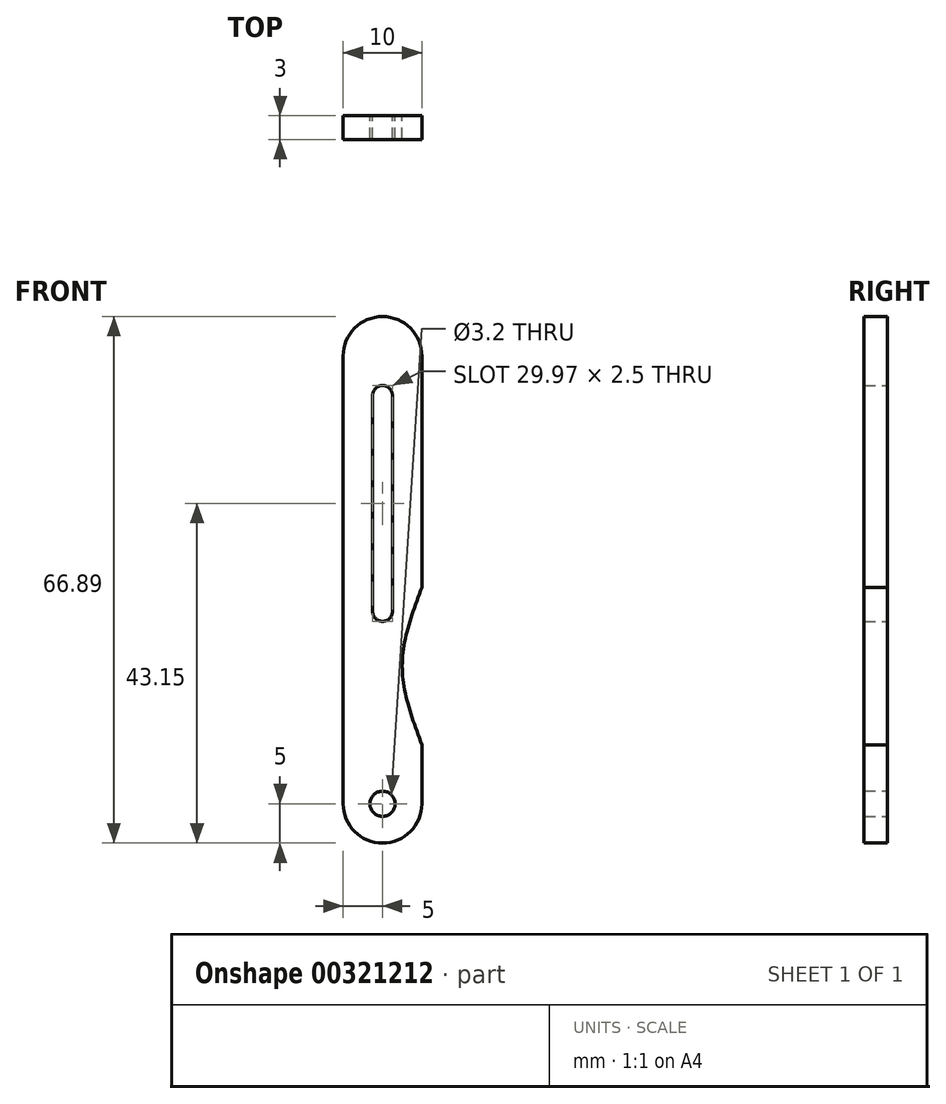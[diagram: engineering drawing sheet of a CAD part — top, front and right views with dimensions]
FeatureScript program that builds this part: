
annotation { "Feature Type Name" : "Feature", "Feature Type Description" : "" }
export const myFeature = defineFeature(function(context is Context, id is Id, definition is map)
    precondition{}
    {
        {
            var Q0;
            Q0=qCreatedBy(makeId("Front.planeOp"),FACE);
            var sketch = newSketch(context, id + "F0", { "sketchPlane" : qUnion([Q0])});
            skCircle(sketch, "E0", {"center": v(0, 17.5) * mm, "radius": 7 * mm, "construction": true});
            skLineSegment(sketch, "E1.bottom", {"start": v(2.5, 27.5) * mm, "end": v(-2.5, 27.5) * mm, "construction": true});
            skLineSegment(sketch, "E1.top", {"start": v(2.5, 7.5) * mm, "end": v(-2.5, 7.5) * mm, "construction": true});
            skLineSegment(sketch, "E1.left", {"start": v(2.5, 27.5) * mm, "end": v(2.5, 7.5) * mm, "construction": true});
            skLineSegment(sketch, "E1.right", {"start": v(-2.5, 27.5) * mm, "end": v(-2.5, 7.5) * mm, "construction": true});
            skFitSpline(sketch, "E2", {"points": [v(-2.5, 27.5) * mm, v(-2.5, 7.5) * mm], "startDerivative": vector(0, -20) * mm, "endDerivative": vector(0, -20) * mm});
            skFitSpline(sketch, "E3", {"points": [v(0, 27.5) * mm, v(-2.5, 17.5) * mm, v(0, 7.5) * mm], "startDerivative": vector(-7.5, -20) * mm, "endDerivative": vector(7.5, -20) * mm});
            skLineSegment(sketch, "E4", {"start": v(0, 27.5) * mm, "end": v(0, 32.5) * mm});
            skLineSegment(sketch, "E5", {"start": v(0, 7.5) * mm, "end": v(0, 0) * mm});
            skArc(sketch, "E6", {"start": v(0, 0) * mm, "mid": v(-5, -5) * mm, "end": v(-10, 0) * mm});
            skCircle(sketch, "E7", {"center": v(0, 38.65) * mm, "radius": 14.15 * mm, "construction": true});
            skLineSegment(sketch, "E8", {"start": v(-5, 25.41) * mm, "end": v(5, 51.89) * mm, "construction": true});
            skLineSegment(sketch, "E9", {"start": v(-14.15, 38.65) * mm, "end": v(14.15, 38.65) * mm, "construction": true});
            skLineSegment(sketch, "E10", {"start": v(-5, 0) * mm, "end": v(-5, 56.89) * mm, "construction": true});
            skArc(sketch, "E11", {"start": v(0, 56.89) * mm, "mid": v(-5, 61.89) * mm, "end": v(-10, 56.89) * mm});
            skLineSegment(sketch, "E12", {"start": v(-10, 56.89) * mm, "end": v(-10, 56.89) * mm});
            skLineSegment(sketch, "E13", {"start": v(0, 56.89) * mm, "end": v(0, 56.89) * mm});
            skLineSegment(sketch, "E14", {"start": v(0, 56.89) * mm, "end": v(0, 32.5) * mm});
            skLineSegment(sketch, "E15", {"start": v(-10, 56.89) * mm, "end": v(-10, 0) * mm});
            skLineSegment(sketch, "E16", {"start": v(-5, 51.89) * mm, "end": v(-5, 24.41) * mm, "construction": true});
            skArc(sketch, "E17.0.startCap", {"start": v(-6.25, 51.89) * mm, "mid": v(-5, 53.14) * mm, "end": v(-3.75, 51.89) * mm});
            skArc(sketch, "E17.0.endCap", {"start": v(-3.75, 24.41) * mm, "mid": v(-5, 23.16) * mm, "end": v(-6.25, 24.41) * mm});
            skLineSegment(sketch, "E17.0.left", {"start": v(-3.75, 51.89) * mm, "end": v(-3.75, 24.41) * mm});
            skLineSegment(sketch, "E17.0.right", {"start": v(-6.25, 51.89) * mm, "end": v(-6.25, 24.41) * mm});
            skCircle(sketch, "E18", {"center": v(-5, 0) * mm, "radius": 1.6 * mm});
            skCircle(sketch, "E19", {"center": v(-5, 0) * mm, "radius": 5 * mm, "construction": true});
            skLineSegment(sketch, "E20", {"start": v(-5, 0) * mm, "end": v(-20.78, 63.66) * mm, "construction": true});
            skPoint(sketch, "E21", {"position": v(0, 24.5) * mm});
            skSolve(sketch);
        }
        {
            var Q0;
            {var subQ0=sQuery(id+"F0.wireOp",EDGE,"E4");Q0=makeQuery(id+"F0.imprint","IMPRINT",FACE,{"disambiguationData":[TD([[makeQuery(id+"F0.imprint","IMPRINT",EDGE,{"derivedFrom":subQ0}),1.0]])]});}
            extrude(context, id + "F1", {"entities" : qUnion([Q0]), "depth" : 3 * mm, "offsetDistance" : 25 * mm});
        }
    });
